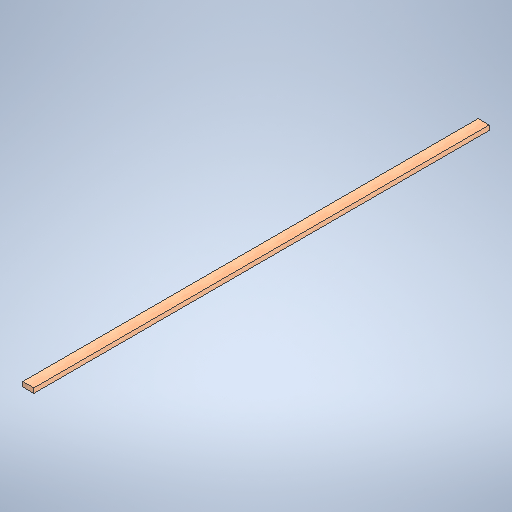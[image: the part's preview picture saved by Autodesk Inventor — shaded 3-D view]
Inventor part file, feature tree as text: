
AUTODESK INVENTOR PART (.ipt)
format: ipt  version: 2025 (Build 290162010, 162A)  size: 270,848 bytes
history: native  units: in
note: dims shown in document units (in); Inventor stores cm internally (conversion verified against a paired STEP export)
features: extrude x1, sketch x1
ambient origin geometry x8: Origin, YZ Plane, XZ Plane, XY Plane, X Axis, Y Axis, Z Axis, Center Point
bodies: Solid1 (feature_tree)
feature tree (2):
  extrude  "Extrusion1"  Depth=1.5in
  sketch  "Sketch1"  dims[d0=3.5in d1=1.5in d2=144.0in d3=0.0in]
